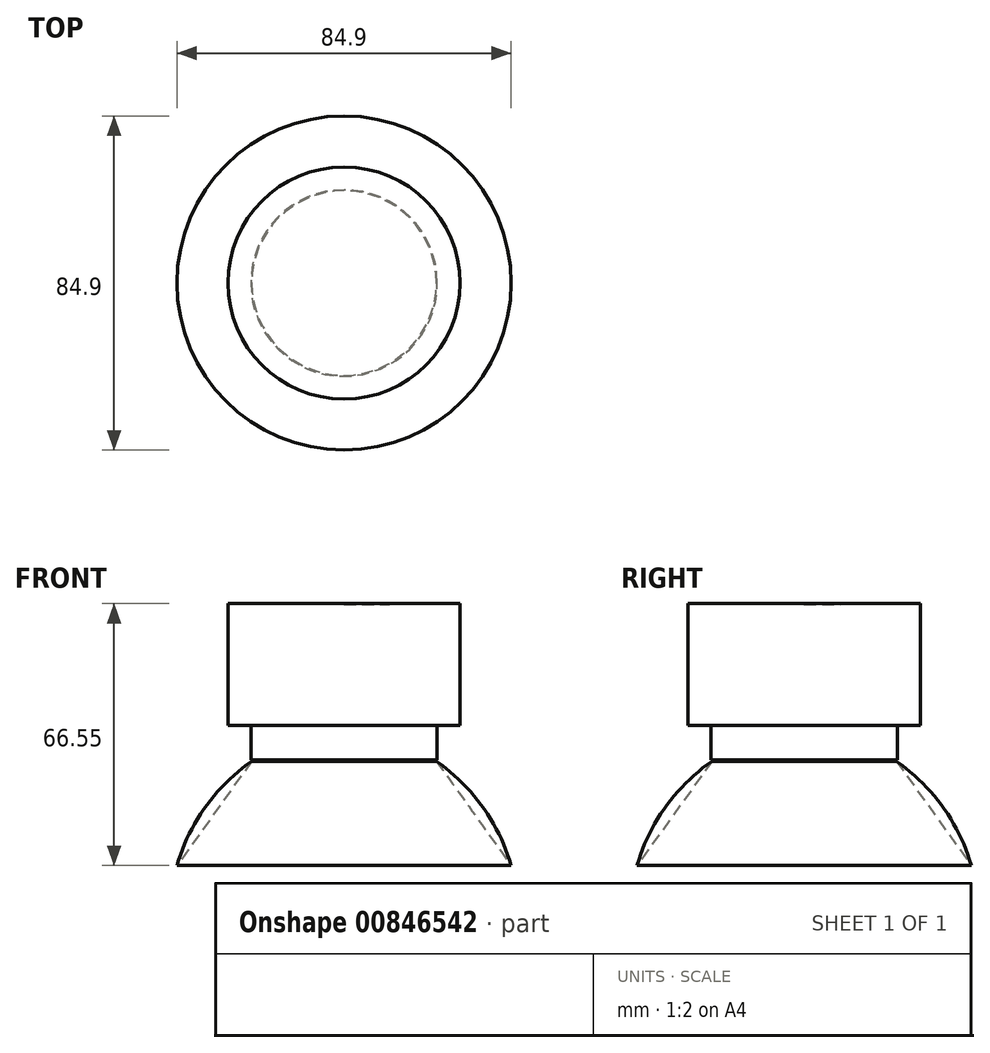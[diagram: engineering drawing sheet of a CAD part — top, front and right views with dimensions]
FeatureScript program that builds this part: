
annotation { "Feature Type Name" : "Feature", "Feature Type Description" : "" }
export const myFeature = defineFeature(function(context is Context, id is Id, definition is map)
    precondition{}
    {
        {
            var Q0;
            Q0=qCreatedBy(makeId("Front.planeOp"),FACE);
            var sketch = newSketch(context, id + "F0", { "sketchPlane" : qUnion([Q0])});
            skLineSegment(sketch, "E0", {"start": v(-29.21, 52.24) * mm, "end": v(-3.3, 52.24) * mm});
            skLineSegment(sketch, "E1", {"start": v(-3.3, 52.24) * mm, "end": v(0, 52.24) * mm});
            skLineSegment(sketch, "E2", {"start": v(0, 52.24) * mm, "end": v(-29.21, 52.24) * mm});
            skLineSegment(sketch, "E3", {"start": v(-29.21, 52.24) * mm, "end": v(-29.21, 21.15) * mm});
            skLineSegment(sketch, "E4", {"start": v(-29.21, 21.15) * mm, "end": v(-23.46, 21.15) * mm});
            skLineSegment(sketch, "E5", {"start": v(-23.46, 21.15) * mm, "end": v(-23.46, 12.52) * mm});
            skLineSegment(sketch, "E6", {"start": v(-23.46, 12.52) * mm, "end": v(0, 12.52) * mm});
            skLineSegment(sketch, "E7", {"start": v(0, 12.52) * mm, "end": v(0, -13.96) * mm});
            skLineSegment(sketch, "E8", {"start": v(0, -13.96) * mm, "end": v(-42.45, -13.96) * mm});
            skLineSegment(sketch, "E9", {"start": v(-42.45, -13.96) * mm, "end": v(-23.46, 12.52) * mm});
            skArc(sketch, "E10", {"start": v(-23.46, 12.52) * mm, "mid": v(-35.24, 0.92) * mm, "end": v(-42.45, -13.96) * mm});
            skSolve(sketch);
        }
        {
            var Q0;
            Q0=makeQuery(id+"F0.imprint","IMPRINT",FACE,{"disambiguationData":[TD([[makeQuery(id+"F0.imprint","IMPRINT",EDGE,{"derivedFrom":sQuery(id+"F0.wireOp",EDGE,"E6")}),-1.0]])]});
            var sketch = newSketch(context, id + "F1", { "sketchPlane" : qUnion([Q0])});
            skLineSegment(sketch, "E11", {"start": v(-29.48, 52.59) * mm, "end": v(-29.48, 21.6) * mm});
            skLineSegment(sketch, "E12", {"start": v(-29.48, 21.6) * mm, "end": v(-23.67, 21.6) * mm});
            skLineSegment(sketch, "E13", {"start": v(-23.67, 21.6) * mm, "end": v(-23.67, 12.9) * mm});
            skLineSegment(sketch, "E14", {"start": v(-23.67, 12.9) * mm, "end": v(0, 12.9) * mm});
            skLineSegment(sketch, "E15", {"start": v(0, 12.9) * mm, "end": v(0, 52.34) * mm});
            skLineSegment(sketch, "E16", {"start": v(0, 52.34) * mm, "end": v(-29.48, 52.59) * mm});
            skSolve(sketch);
        }
        {
            var Q0;
            Q0=makeQuery(id+"F1.imprint","IMPRINT",FACE,{"disambiguationData":[TD([[makeQuery(id+"F1.imprint","IMPRINT",EDGE,{"derivedFrom":makeQuery(id+"F0.imprint","IMPRINT",EDGE,{"derivedFrom":sQuery(id+"F0.wireOp",EDGE,"E6")})}),-1.0]])]});
            var Q1;
            Q1=makeQuery(id+"F0.imprint","IMPRINT",FACE,{"disambiguationData":[TD([[makeQuery(id+"F0.imprint","IMPRINT",EDGE,{"derivedFrom":sQuery(id+"F0.wireOp",EDGE,"E9")}),1.0]])]});
            var Q2;
            Q2=makeQuery(id+"F1.imprint","IMPRINT",FACE,{"disambiguationData":[TD([[makeQuery(id+"F1.imprint","IMPRINT",EDGE,{"derivedFrom":sQuery(id+"F1.wireOp",EDGE,"E11")}),1.0]])]});
            var Q3;
            Q3=sQuery(id+"F0.wireOp",EDGE,"E7");
            revolve(context, id + "F2", {"surfaceOperationType" : NewSurfaceOperationType.NEW, "entities" : qUnion([Q0, Q1, Q2]), "axis" : qUnion([Q3]), "revolveType" : RevolveType.FULL});
        }
    });
